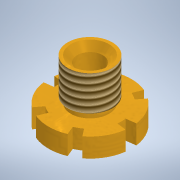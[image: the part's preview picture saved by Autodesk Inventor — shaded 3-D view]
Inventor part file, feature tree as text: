
AUTODESK INVENTOR PART (.ipt)
format: ipt  version: 2020 (Build 240168000, 168)  size: 190,976 bytes
history: native  units: mm
features: sketch x4, extrude x3, hole x1, thread x1, projected_geometry x1
ambient origin geometry x8: Origin, YZ Plane, XZ Plane, XY Plane, X Axis, Y Axis, Z Axis, Center Point
bodies: Solid1 (feature_tree)
feature tree (10):
  extrude  "Extrusion1"  Depth=10.0mm
  extrude  "Extrusion2"  Depth=1.308997mm
  extrude  "Extrusion3"  Depth=1.308997mm
  hole  "Hole1"  [1 undecoded]
  thread  "Thread1"  [1 undecoded]
  sketch  "Sketch1"  dims[d0=13.0mm d1=10.0mm]
  sketch  "Sketch2"  dims[d2=6.554mm d3=1.308997mm]
  projected_geometry  "Projected Loop1"
  sketch  "Sketch3"  dims[d4=7.0mm d5=1.308997mm]
  sketch  "Sketch4"  dims[d6=60.0mm d8=360.0deg d10=3.0mm d11=0.0mm d12=6.0mm d13=1.0mm d14=0.0mm d15=7.0mm d16=5.5mm d17=0.0mm d18=4.0mm d19=8.60806mm d20=6.0mm d21=2.0mm d22=90.0deg d23=8.0mm d24=20.594885mm d25=10.0mm d26=0.0mm]
note: 2 required parameter values undecoded (feature->parameter linkage not recoverable at this tier; creation-order binding heuristic only, values carry confidence <= 0.55)
